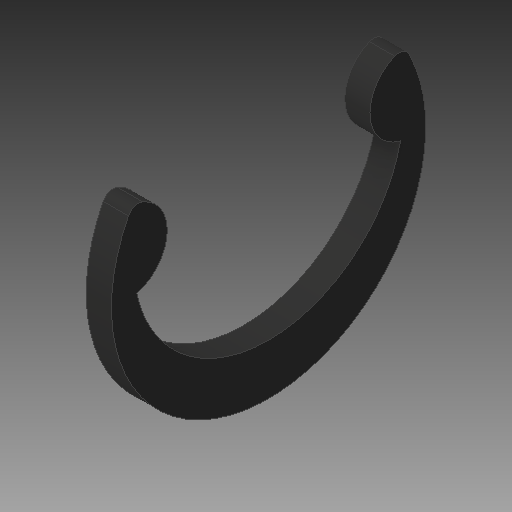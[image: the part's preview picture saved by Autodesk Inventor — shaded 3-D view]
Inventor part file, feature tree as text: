
AUTODESK INVENTOR PART (.ipt)
format: ipt  version: 2018 (Build 220112000, 112)  size: 95,744 bytes
history: native  units: in
note: dims shown in document units (in); Inventor stores cm internally (conversion verified against a paired STEP export)
features: extrude x1
ambient origin geometry x8: Origin, YZ Plane, XZ Plane, XY Plane, X Axis, Y Axis, Z Axis, Center Point
bodies: Solid1 (feature_tree)
feature tree (1):
  extrude  "Extrude1"  [1 undecoded]
note: 1 required parameter value undecoded (feature->parameter linkage not recoverable at this tier; creation-order binding heuristic only, values carry confidence <= 0.55)
